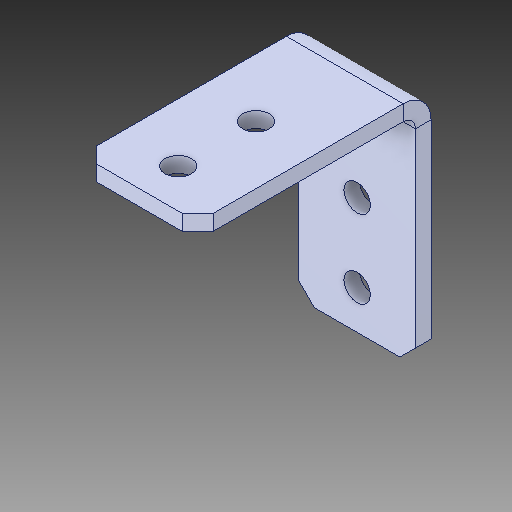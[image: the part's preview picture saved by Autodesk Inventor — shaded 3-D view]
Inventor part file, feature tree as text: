
AUTODESK INVENTOR PART (.ipt)
format: ipt  version: 2017 (Build 210142000, 142)  size: 121,344 bytes
history: native  units: in
note: dims shown in document units (in); Inventor stores cm internally (conversion verified against a paired STEP export)
features: chamfer x1
ambient origin geometry x8: Origin, YZ Plane, XZ Plane, XY Plane, X Axis, Y Axis, Z Axis, Center Point
bodies: Solid1 (feature_tree)
feature tree (1):
  chamfer  "Chamfer1"  [1 undecoded]
note: 1 required parameter value undecoded (feature->parameter linkage not recoverable at this tier; creation-order binding heuristic only, values carry confidence <= 0.55)
